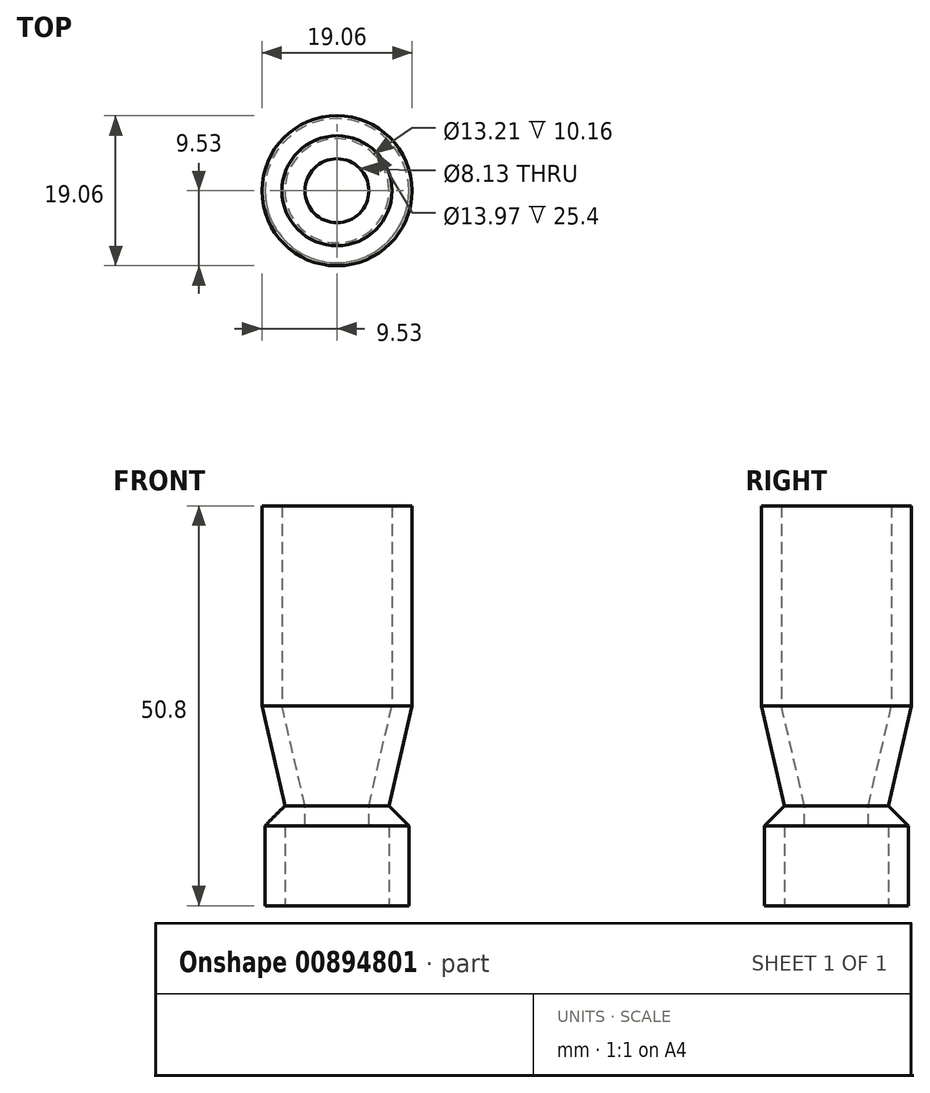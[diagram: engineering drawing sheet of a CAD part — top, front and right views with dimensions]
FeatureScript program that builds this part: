
annotation { "Feature Type Name" : "Feature", "Feature Type Description" : "" }
export const myFeature = defineFeature(function(context is Context, id is Id, definition is map)
    precondition{}
    {
        {
            var Q0;
            Q0=qCreatedBy(makeId("Top.planeOp"),FACE);
            var sketch = newSketch(context, id + "F0", { "sketchPlane" : qUnion([Q0])});
            skCircle(sketch, "E0", {"center": v(0, 0) * mm, "radius": 6.6 * mm});
            skCircle(sketch, "E1", {"center": v(0, 0) * mm, "radius": 9.14 * mm});
            skSolve(sketch);
        }
        {
            var Q0;
            Q0=makeQuery(id+"F0.imprint","IMPRINT",FACE,{"disambiguationData":[TD([[makeQuery(id+"F0.imprint","IMPRINT",EDGE,{"derivedFrom":sQuery(id+"F0.wireOp",EDGE,"E0")}),-1.0]])]});
            extrude(context, id + "F1", {"entities" : qUnion([Q0]), "depth" : 12.7 * mm, "offsetDistance" : 25.4 * mm});
        }
        {
            var Q0;
            Q0=qCreatedBy(makeId("Right.planeOp"),FACE);
            var sketch = newSketch(context, id + "F2", { "sketchPlane" : qUnion([Q0])});
            skLineSegment(sketch, "E2", {"start": v(-6.6, 12.7) * mm, "end": v(-9.53, 25.4) * mm});
            skLineSegment(sketch, "E3", {"start": v(-9.53, 25.4) * mm, "end": v(-6.99, 25.4) * mm});
            skLineSegment(sketch, "E4", {"start": v(-6.99, 25.4) * mm, "end": v(-4.06, 12.7) * mm});
            skLineSegment(sketch, "E5", {"start": v(-4.06, 12.7) * mm, "end": v(-6.6, 12.7) * mm});
            skLineSegment(sketch, "E6", {"start": v(-9.53, 25.4) * mm, "end": v(-9.53, 50.8) * mm});
            skLineSegment(sketch, "E7", {"start": v(-9.53, 50.8) * mm, "end": v(-6.99, 50.8) * mm});
            skLineSegment(sketch, "E8", {"start": v(-6.99, 50.8) * mm, "end": v(-6.99, 25.4) * mm});
            skSolve(sketch);
        }
        {
            var Q0;
            Q0=qCreatedBy(makeId("Top.planeOp"),FACE);
            cPlane(context, id + "F3", {"entities" : qUnion([Q0]), "cplaneType" : CPlaneType.OFFSET, "offset" : 12.7 * mm, "width" : 152.4 * mm, "height" : 152.4 * mm});
        }
        {
            var Q0;
            Q0=qCreatedBy(id+"F3.planeOp",FACE);
            var sketch = newSketch(context, id + "F4", { "sketchPlane" : qUnion([Q0])});
            skCircle(sketch, "E9", {"center": v(0, 0) * mm, "radius": 6.6 * mm});
            skCircle(sketch, "E10", {"center": v(0, 0) * mm, "radius": 4.06 * mm});
            skSolve(sketch);
        }
        {
            var Q0;
            Q0=makeQuery(id+"F4.imprint","IMPRINT",FACE,{"disambiguationData":[TD([[makeQuery(id+"F4.imprint","IMPRINT",EDGE,{"derivedFrom":sQuery(id+"F4.wireOp",EDGE,"E9")}),1.0]])]});
            extrude(context, id + "F5", {"entities" : qUnion([Q0]), "operationType" : NewBodyOperationType.ADD, "oppositeDirection" : true, "depth" : 2.54 * mm, "offsetDistance" : 25.4 * mm});
        }
        {
            var Q0;
            Q0=makeQuery(id+"F2.imprint","IMPRINT",FACE,{"disambiguationData":[TD([[makeQuery(id+"F2.imprint","IMPRINT",EDGE,{"derivedFrom":sQuery(id+"F2.wireOp",EDGE,"E2")}),-1.0]])]});
            var Q1;
            Q1=makeQuery(id+"F2.imprint","IMPRINT",FACE,{"disambiguationData":[TD([[makeQuery(id+"F2.imprint","IMPRINT",EDGE,{"derivedFrom":sQuery(id+"F2.wireOp",EDGE,"E3")}),1.0]])]});
            var Q2;
            Q2=makeQuery(id+"F1.opExtrude","CAP_EDGE",EDGE,{"disambiguationData":[OSD([sQuery(id+"F0.wireOp",EDGE,"E0")])],"isStart":true});
            revolve(context, id + "F6", {"operationType" : NewBodyOperationType.ADD, "surfaceOperationType" : NewSurfaceOperationType.NEW, "entities" : qUnion([Q0, Q1]), "axis" : qUnion([Q2]), "revolveType" : RevolveType.FULL});
        }
        {
            var Q0;
            Q0=makeQuery(id+"F1.opExtrude","CAP_EDGE",EDGE,{"disambiguationData":[OSD([sQuery(id+"F0.wireOp",EDGE,"E1")])],"isStart":false});
            chamfer(context, id + "F7", {"entities" : qUnion([Q0]), "width" : 2.54 * mm, "tangentPropagation" : true});
        }
    });
